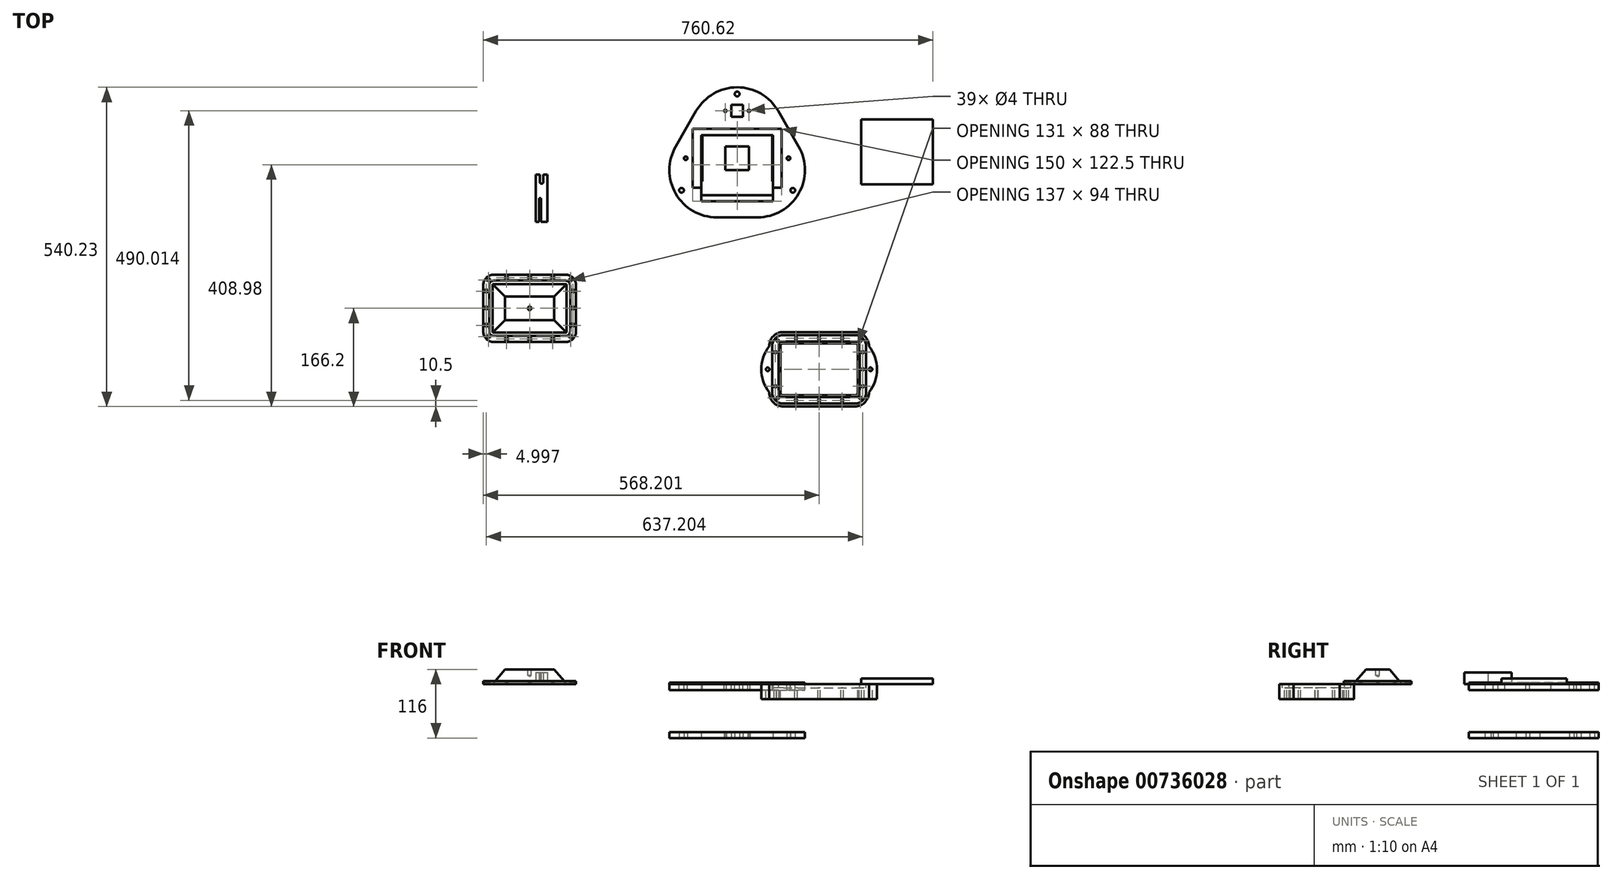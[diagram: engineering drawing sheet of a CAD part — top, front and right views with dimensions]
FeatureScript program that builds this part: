
annotation { "Feature Type Name" : "Feature", "Feature Type Description" : "" }
export const myFeature = defineFeature(function(context is Context, id is Id, definition is map)
    precondition{}
    {
        {
            var Q0;
            Q0=qCreatedBy(makeId("Top.planeOp"),FACE);
            var sketch = newSketch(context, id + "F0", { "sketchPlane" : qUnion([Q0])});
            skLineSegment(sketch, "E0.bottom", {"start": v(-60.5, 39) * mm, "end": v(60.5, 39) * mm});
            skLineSegment(sketch, "E0.top", {"start": v(-60.5, -39) * mm, "end": v(60.5, -39) * mm});
            skLineSegment(sketch, "E0.left", {"start": v(-60.5, 39) * mm, "end": v(-60.5, -39) * mm});
            skLineSegment(sketch, "E0.right", {"start": v(60.5, 39) * mm, "end": v(60.5, -39) * mm});
            skLineSegment(sketch, "E1.bottom", {"start": v(75, -50) * mm, "end": v(-75, -50) * mm});
            skLineSegment(sketch, "E1.top", {"start": v(75, 50) * mm, "end": v(-75, 50) * mm});
            skLineSegment(sketch, "E1.left", {"start": v(75, -50) * mm, "end": v(75, 50) * mm});
            skLineSegment(sketch, "E1.right", {"start": v(-75, -50) * mm, "end": v(-75, 50) * mm});
            skCircle(sketch, "E2.cCircle", {"center": v(0, 0) * mm, "radius": 100 * mm, "construction": true});
            skLineSegment(sketch, "E2.0", {"start": v(34.64, -100) * mm, "end": v(-34.64, -100) * mm});
            skLineSegment(sketch, "E2.1", {"start": v(-103.92, 20) * mm, "end": v(-69.28, 80) * mm});
            skLineSegment(sketch, "E2.2", {"start": v(69.28, 80) * mm, "end": v(103.92, 20) * mm});
            skPoint(sketch, "E2.0.midPoint", {"position": v(0, -100) * mm});
            skPoint(sketch, "E3.visualSharp", {"position": v(-173.2, -100) * mm});
            skArc(sketch, "E3.filletArc", {"start": v(-103.92, 20) * mm, "mid": v(-103.92, -60) * mm, "end": v(-34.64, -100) * mm});
            skPoint(sketch, "E4.visualSharp", {"position": v(0, 200) * mm});
            skArc(sketch, "E4.filletArc", {"start": v(69.28, 80) * mm, "mid": v(0, 120) * mm, "end": v(-69.28, 80) * mm});
            skPoint(sketch, "E5.visualSharp", {"position": v(173.2, -100) * mm});
            skArc(sketch, "E5.filletArc", {"start": v(34.64, -100) * mm, "mid": v(103.92, -60) * mm, "end": v(103.92, 20) * mm});
            skLineSegment(sketch, "E6.bottom", {"start": v(10, 90.28) * mm, "end": v(-10, 90.28) * mm});
            skLineSegment(sketch, "E6.top", {"start": v(10, 70.28) * mm, "end": v(-10, 70.28) * mm});
            skLineSegment(sketch, "E6.left", {"start": v(10, 90.28) * mm, "end": v(10, 70.28) * mm});
            skLineSegment(sketch, "E6.right", {"start": v(-10, 90.28) * mm, "end": v(-10, 70.28) * mm});
            skPoint(sketch, "E6.middle", {"position": v(0, 80.28) * mm});
            skLineSegment(sketch, "E7", {"start": v(-57.27, -42.57) * mm, "end": v(57.28, -42.57) * mm, "construction": true});
            skLineSegment(sketch, "E8", {"start": v(0, -42.57) * mm, "end": v(0, -39) * mm, "construction": true});
            skLineSegment(sketch, "E9.0", {"start": v(-59, 39) * mm, "end": v(-59, -39) * mm});
            skLineSegment(sketch, "E10.0", {"start": v(59, 39) * mm, "end": v(59, -39) * mm});
            skCircle(sketch, "E11", {"center": v(87, 0) * mm, "radius": 3 * mm});
            skLineSegment(sketch, "E12.bottom", {"start": v(210.03, 65.62) * mm, "end": v(331.03, 65.62) * mm});
            skLineSegment(sketch, "E12.top", {"start": v(210.03, -44.38) * mm, "end": v(331.03, -44.38) * mm});
            skLineSegment(sketch, "E12.left", {"start": v(210.03, 65.62) * mm, "end": v(210.03, -44.38) * mm});
            skLineSegment(sketch, "E12.right", {"start": v(331.03, 65.62) * mm, "end": v(331.03, -44.38) * mm});
            skLineSegment(sketch, "E13.bottom", {"start": v(78.11, -313.23) * mm, "end": v(199.11, -313.23) * mm});
            skLineSegment(sketch, "E13.top", {"start": v(78.11, -401.23) * mm, "end": v(199.11, -401.23) * mm});
            skLineSegment(sketch, "E13.left", {"start": v(73.11, -318.23) * mm, "end": v(73.11, -396.23) * mm});
            skLineSegment(sketch, "E13.right", {"start": v(204.11, -318.23) * mm, "end": v(204.11, -396.23) * mm});
            skCircle(sketch, "E14", {"center": v(225.61, -357.23) * mm, "radius": 3 * mm});
            skPoint(sketch, "E14.centerSnap0", {"position": v(204.11, -357.23) * mm});
            skPoint(sketch, "E15", {"position": v(138.61, -357.23) * mm});
            skPoint(sketch, "E15.positionSnap0", {"position": v(138.61, -313.23) * mm});
            skPoint(sketch, "E15.positionSnap1", {"position": v(73.11, -357.23) * mm});
            skPoint(sketch, "E16.visualSharp", {"position": v(73.11, -313.23) * mm});
            skArc(sketch, "E16.filletArc", {"start": v(78.11, -313.23) * mm, "mid": v(74.58, -314.7) * mm, "end": v(73.11, -318.23) * mm});
            skPoint(sketch, "E17.visualSharp", {"position": v(73.11, -401.23) * mm});
            skArc(sketch, "E17.filletArc", {"start": v(73.11, -396.23) * mm, "mid": v(74.58, -399.77) * mm, "end": v(78.11, -401.23) * mm});
            skPoint(sketch, "E18.visualSharp", {"position": v(204.11, -401.23) * mm});
            skArc(sketch, "E18.filletArc", {"start": v(199.11, -401.23) * mm, "mid": v(202.65, -399.77) * mm, "end": v(204.11, -396.23) * mm});
            skPoint(sketch, "E19.visualSharp", {"position": v(204.11, -313.23) * mm});
            skArc(sketch, "E19.filletArc", {"start": v(204.11, -318.23) * mm, "mid": v(202.65, -314.7) * mm, "end": v(199.11, -313.23) * mm});
            skArc(sketch, "E20.0", {"start": v(78.11, -310.23) * mm, "mid": v(72.45, -312.57) * mm, "end": v(70.11, -318.23) * mm});
            skLineSegment(sketch, "E20.1", {"start": v(70.11, -318.23) * mm, "end": v(70.11, -396.23) * mm});
            skLineSegment(sketch, "E20.2", {"start": v(78.11, -310.23) * mm, "end": v(199.11, -310.23) * mm});
            skArc(sketch, "E20.3", {"start": v(70.11, -396.23) * mm, "mid": v(72.45, -401.89) * mm, "end": v(78.11, -404.23) * mm});
            skArc(sketch, "E20.4", {"start": v(207.11, -318.23) * mm, "mid": v(204.77, -312.57) * mm, "end": v(199.11, -310.23) * mm});
            skLineSegment(sketch, "E20.5", {"start": v(207.11, -318.23) * mm, "end": v(207.11, -396.23) * mm});
            skArc(sketch, "E20.6", {"start": v(199.11, -404.23) * mm, "mid": v(204.77, -401.89) * mm, "end": v(207.11, -396.23) * mm});
            skLineSegment(sketch, "E20.7", {"start": v(78.11, -404.23) * mm, "end": v(199.11, -404.23) * mm});
            skArc(sketch, "E21.0", {"start": v(78.11, -299.23) * mm, "mid": v(64.68, -304.8) * mm, "end": v(59.11, -318.23) * mm});
            skLineSegment(sketch, "E21.1", {"start": v(59.11, -318.23) * mm, "end": v(59.11, -396.23) * mm});
            skLineSegment(sketch, "E21.2", {"start": v(78.11, -299.23) * mm, "end": v(199.11, -299.23) * mm});
            skArc(sketch, "E21.3", {"start": v(59.11, -396.23) * mm, "mid": v(64.68, -409.66) * mm, "end": v(78.11, -415.23) * mm});
            skArc(sketch, "E21.4", {"start": v(218.11, -318.23) * mm, "mid": v(212.55, -304.8) * mm, "end": v(199.11, -299.23) * mm});
            skLineSegment(sketch, "E21.5", {"start": v(218.11, -318.23) * mm, "end": v(218.11, -396.23) * mm});
            skArc(sketch, "E21.6", {"start": v(199.11, -415.23) * mm, "mid": v(212.55, -409.66) * mm, "end": v(218.11, -396.23) * mm});
            skLineSegment(sketch, "E21.7", {"start": v(78.11, -415.23) * mm, "end": v(199.11, -415.23) * mm});
            skArc(sketch, "E22.0", {"start": v(78.11, -294.23) * mm, "mid": v(61.14, -301.26) * mm, "end": v(54.11, -318.23) * mm});
            skLineSegment(sketch, "E22.1", {"start": v(54.11, -318.23) * mm, "end": v(54.11, -396.23) * mm});
            skLineSegment(sketch, "E22.2", {"start": v(78.11, -294.23) * mm, "end": v(199.11, -294.23) * mm});
            skArc(sketch, "E22.3", {"start": v(54.11, -396.23) * mm, "mid": v(61.14, -413.2) * mm, "end": v(78.11, -420.23) * mm});
            skArc(sketch, "E22.4", {"start": v(223.11, -318.23) * mm, "mid": v(216.08, -301.26) * mm, "end": v(199.11, -294.23) * mm});
            skLineSegment(sketch, "E22.5", {"start": v(223.11, -318.23) * mm, "end": v(223.11, -396.23) * mm});
            skArc(sketch, "E22.6", {"start": v(199.11, -420.23) * mm, "mid": v(216.08, -413.2) * mm, "end": v(223.11, -396.23) * mm});
            skLineSegment(sketch, "E22.7", {"start": v(78.11, -420.23) * mm, "end": v(199.11, -420.23) * mm});
            skArc(sketch, "E23", {"start": v(223.11, -396.23) * mm, "mid": v(236.56, -357.23) * mm, "end": v(223.11, -318.23) * mm});
            skLineSegment(sketch, "E24", {"start": v(138.61, -357.23) * mm, "end": v(138.61, -335.81) * mm, "construction": true});
            skCircle(sketch, "E25.MirrorC", {"center": v(51.61, -357.23) * mm, "radius": 3 * mm});
            skArc(sketch, "E26.MirrorCS", {"start": v(54.11, -396.23) * mm, "mid": v(40.66, -357.23) * mm, "end": v(54.11, -318.23) * mm});
            skArc(sketch, "E27.0", {"start": v(212.61, -318.23) * mm, "mid": v(208.66, -308.68) * mm, "end": v(199.11, -304.73) * mm, "construction": true});
            skLineSegment(sketch, "E27.1", {"start": v(78.11, -304.73) * mm, "end": v(138.61, -304.73) * mm, "construction": true});
            skLineSegment(sketch, "E27.2", {"start": v(212.61, -318.23) * mm, "end": v(212.61, -357.23) * mm, "construction": true});
            skArc(sketch, "E27.3", {"start": v(78.11, -304.73) * mm, "mid": v(68.56, -308.68) * mm, "end": v(64.61, -318.23) * mm, "construction": true});
            skArc(sketch, "E27.4", {"start": v(199.11, -409.73) * mm, "mid": v(208.66, -405.78) * mm, "end": v(212.61, -396.23) * mm, "construction": true});
            skLineSegment(sketch, "E27.5", {"start": v(78.11, -409.73) * mm, "end": v(138.61, -409.73) * mm, "construction": true});
            skArc(sketch, "E27.6", {"start": v(64.61, -396.23) * mm, "mid": v(68.56, -405.78) * mm, "end": v(78.11, -409.73) * mm, "construction": true});
            skLineSegment(sketch, "E27.7", {"start": v(64.61, -318.23) * mm, "end": v(64.61, -357.23) * mm, "construction": true});
            skPoint(sketch, "E28", {"position": v(208.66, -405.78) * mm});
            skPoint(sketch, "E29", {"position": v(212.61, -357.23) * mm});
            skPoint(sketch, "E30", {"position": v(138.61, -409.73) * mm});
            skPoint(sketch, "E31", {"position": v(64.61, -357.23) * mm});
            skPoint(sketch, "E32", {"position": v(68.56, -405.78) * mm});
            skPoint(sketch, "E33", {"position": v(208.66, -308.68) * mm});
            skPoint(sketch, "E34", {"position": v(68.56, -308.68) * mm});
            skPoint(sketch, "E35", {"position": v(138.61, -304.73) * mm});
            skLineSegment(sketch, "E36", {"start": v(64.61, -357.23) * mm, "end": v(64.61, -396.23) * mm, "construction": true});
            skLineSegment(sketch, "E37", {"start": v(138.61, -409.73) * mm, "end": v(199.11, -409.73) * mm, "construction": true});
            skLineSegment(sketch, "E38", {"start": v(212.61, -357.23) * mm, "end": v(212.61, -396.23) * mm, "construction": true});
            skLineSegment(sketch, "E39", {"start": v(138.61, -304.73) * mm, "end": v(199.11, -304.73) * mm, "construction": true});
            skPoint(sketch, "E40", {"position": v(177.68, -304.73) * mm});
            skPoint(sketch, "E41.MirrorP", {"position": v(99.54, -304.73) * mm});
            skLineSegment(sketch, "E42", {"start": v(138.61, -357.23) * mm, "end": v(162.86, -357.23) * mm, "construction": true});
            skPoint(sketch, "E43", {"position": v(212.61, -328.33) * mm});
            skPoint(sketch, "E44.MirrorP", {"position": v(212.61, -386.12) * mm});
            skPoint(sketch, "E45.MirrorP", {"position": v(177.68, -409.73) * mm});
            skPoint(sketch, "E46.MirrorP", {"position": v(99.54, -409.73) * mm});
            skPoint(sketch, "E47.MirrorP", {"position": v(64.61, -328.33) * mm});
            skPoint(sketch, "E48.MirrorP", {"position": v(64.61, -386.12) * mm});
            skLineSegment(sketch, "E49.bottom", {"start": v(-411.6, -210.03) * mm, "end": v(-290.6, -210.03) * mm});
            skLineSegment(sketch, "E49.top", {"start": v(-411.6, -298.03) * mm, "end": v(-290.6, -298.03) * mm});
            skLineSegment(sketch, "E49.left", {"start": v(-416.6, -215.03) * mm, "end": v(-416.6, -293.03) * mm});
            skLineSegment(sketch, "E49.right", {"start": v(-285.6, -215.03) * mm, "end": v(-285.6, -293.03) * mm});
            skCircle(sketch, "E50", {"center": v(-264.1, -254.03) * mm, "radius": 3 * mm});
            skPoint(sketch, "E50.centerSnap0", {"position": v(-285.6, -254.03) * mm});
            skPoint(sketch, "E51", {"position": v(-351.1, -254.03) * mm});
            skPoint(sketch, "E51.positionSnap0", {"position": v(-351.1, -210.03) * mm});
            skPoint(sketch, "E51.positionSnap1", {"position": v(-416.6, -254.03) * mm});
            skPoint(sketch, "E52.visualSharp", {"position": v(-416.6, -210.03) * mm});
            skArc(sketch, "E52.filletArc", {"start": v(-411.6, -210.03) * mm, "mid": v(-415.13, -211.5) * mm, "end": v(-416.6, -215.03) * mm});
            skPoint(sketch, "E53.visualSharp", {"position": v(-416.6, -298.03) * mm});
            skArc(sketch, "E53.filletArc", {"start": v(-416.6, -293.03) * mm, "mid": v(-415.13, -296.57) * mm, "end": v(-411.6, -298.03) * mm});
            skPoint(sketch, "E54.visualSharp", {"position": v(-285.6, -298.03) * mm});
            skArc(sketch, "E54.filletArc", {"start": v(-290.6, -298.03) * mm, "mid": v(-287.06, -296.57) * mm, "end": v(-285.6, -293.03) * mm});
            skPoint(sketch, "E55.visualSharp", {"position": v(-285.6, -210.03) * mm});
            skArc(sketch, "E55.filletArc", {"start": v(-285.6, -215.03) * mm, "mid": v(-287.06, -211.5) * mm, "end": v(-290.6, -210.03) * mm});
            skArc(sketch, "E56.0", {"start": v(-411.6, -207.03) * mm, "mid": v(-417.25, -209.37) * mm, "end": v(-419.6, -215.03) * mm});
            skLineSegment(sketch, "E56.1", {"start": v(-419.6, -215.03) * mm, "end": v(-419.6, -293.03) * mm});
            skLineSegment(sketch, "E56.2", {"start": v(-411.6, -207.03) * mm, "end": v(-290.6, -207.03) * mm});
            skArc(sketch, "E56.3", {"start": v(-419.6, -293.03) * mm, "mid": v(-417.25, -298.69) * mm, "end": v(-411.6, -301.03) * mm});
            skArc(sketch, "E56.4", {"start": v(-282.6, -215.03) * mm, "mid": v(-284.94, -209.37) * mm, "end": v(-290.6, -207.03) * mm});
            skLineSegment(sketch, "E56.5", {"start": v(-282.6, -215.03) * mm, "end": v(-282.6, -293.03) * mm});
            skArc(sketch, "E56.6", {"start": v(-290.6, -301.03) * mm, "mid": v(-284.94, -298.69) * mm, "end": v(-282.6, -293.03) * mm});
            skLineSegment(sketch, "E56.7", {"start": v(-411.6, -301.03) * mm, "end": v(-290.6, -301.03) * mm});
            skArc(sketch, "E57.0", {"start": v(-411.6, -197.03) * mm, "mid": v(-424.32, -202.3) * mm, "end": v(-429.6, -215.03) * mm});
            skLineSegment(sketch, "E57.1", {"start": v(-429.6, -215.03) * mm, "end": v(-429.6, -293.03) * mm});
            skLineSegment(sketch, "E57.2", {"start": v(-411.6, -197.03) * mm, "end": v(-290.6, -197.03) * mm});
            skArc(sketch, "E57.3", {"start": v(-429.6, -293.03) * mm, "mid": v(-424.32, -305.76) * mm, "end": v(-411.6, -311.03) * mm});
            skArc(sketch, "E57.4", {"start": v(-272.6, -215.03) * mm, "mid": v(-277.87, -202.3) * mm, "end": v(-290.6, -197.03) * mm});
            skLineSegment(sketch, "E57.5", {"start": v(-272.6, -215.03) * mm, "end": v(-272.6, -293.03) * mm});
            skArc(sketch, "E57.6", {"start": v(-290.6, -311.03) * mm, "mid": v(-277.87, -305.76) * mm, "end": v(-272.6, -293.03) * mm});
            skLineSegment(sketch, "E57.7", {"start": v(-411.6, -311.03) * mm, "end": v(-290.6, -311.03) * mm});
            skArc(sketch, "E58.0", {"start": v(-411.6, -192.03) * mm, "mid": v(-427.86, -198.77) * mm, "end": v(-434.6, -215.03) * mm});
            skLineSegment(sketch, "E58.1", {"start": v(-434.6, -215.03) * mm, "end": v(-434.6, -293.03) * mm});
            skLineSegment(sketch, "E58.2", {"start": v(-411.6, -192.03) * mm, "end": v(-290.6, -192.03) * mm});
            skArc(sketch, "E58.3", {"start": v(-434.6, -293.03) * mm, "mid": v(-427.86, -309.3) * mm, "end": v(-411.6, -316.03) * mm});
            skArc(sketch, "E58.4", {"start": v(-267.6, -215.03) * mm, "mid": v(-274.33, -198.77) * mm, "end": v(-290.6, -192.03) * mm});
            skLineSegment(sketch, "E58.5", {"start": v(-267.6, -215.03) * mm, "end": v(-267.6, -293.03) * mm});
            skArc(sketch, "E58.6", {"start": v(-290.6, -316.03) * mm, "mid": v(-274.33, -309.3) * mm, "end": v(-267.6, -293.03) * mm});
            skLineSegment(sketch, "E58.7", {"start": v(-411.6, -316.03) * mm, "end": v(-290.6, -316.03) * mm});
            skArc(sketch, "E59", {"start": v(-267.6, -293.03) * mm, "mid": v(-254.14, -254.03) * mm, "end": v(-267.6, -215.03) * mm});
            skLineSegment(sketch, "E60", {"start": v(-351.1, -254.03) * mm, "end": v(-351.1, -232.61) * mm, "construction": true});
            skCircle(sketch, "E61.MirrorC", {"center": v(-438.1, -254.03) * mm, "radius": 3 * mm});
            skArc(sketch, "E62.MirrorCS", {"start": v(-434.6, -293.03) * mm, "mid": v(-448.04, -254.03) * mm, "end": v(-434.6, -215.03) * mm});
            skArc(sketch, "E63.0", {"start": v(-277.6, -215.03) * mm, "mid": v(-281.4, -205.84) * mm, "end": v(-290.6, -202.03) * mm, "construction": true});
            skLineSegment(sketch, "E63.1", {"start": v(-411.6, -202.03) * mm, "end": v(-351.1, -202.03) * mm, "construction": true});
            skLineSegment(sketch, "E63.2", {"start": v(-277.6, -215.03) * mm, "end": v(-277.6, -254.03) * mm, "construction": true});
            skArc(sketch, "E63.3", {"start": v(-411.6, -202.03) * mm, "mid": v(-420.79, -205.84) * mm, "end": v(-424.6, -215.03) * mm, "construction": true});
            skArc(sketch, "E63.4", {"start": v(-290.6, -306.03) * mm, "mid": v(-281.4, -302.22) * mm, "end": v(-277.6, -293.03) * mm, "construction": true});
            skLineSegment(sketch, "E63.5", {"start": v(-411.6, -306.03) * mm, "end": v(-351.1, -306.03) * mm, "construction": true});
            skArc(sketch, "E63.6", {"start": v(-424.6, -293.03) * mm, "mid": v(-420.79, -302.22) * mm, "end": v(-411.6, -306.03) * mm, "construction": true});
            skLineSegment(sketch, "E63.7", {"start": v(-424.6, -215.03) * mm, "end": v(-424.6, -254.03) * mm, "construction": true});
            skPoint(sketch, "E64", {"position": v(-281.4, -302.22) * mm});
            skPoint(sketch, "E65", {"position": v(-277.6, -254.03) * mm});
            skPoint(sketch, "E66", {"position": v(-351.1, -306.03) * mm});
            skPoint(sketch, "E67", {"position": v(-424.6, -254.03) * mm});
            skPoint(sketch, "E68", {"position": v(-420.79, -302.22) * mm});
            skPoint(sketch, "E69", {"position": v(-281.4, -205.84) * mm});
            skPoint(sketch, "E70", {"position": v(-420.79, -205.84) * mm});
            skPoint(sketch, "E71", {"position": v(-351.1, -202.03) * mm});
            skLineSegment(sketch, "E72", {"start": v(-424.6, -254.03) * mm, "end": v(-424.6, -293.03) * mm, "construction": true});
            skLineSegment(sketch, "E73", {"start": v(-351.1, -306.03) * mm, "end": v(-290.6, -306.03) * mm, "construction": true});
            skLineSegment(sketch, "E74", {"start": v(-277.6, -254.03) * mm, "end": v(-277.6, -293.03) * mm, "construction": true});
            skLineSegment(sketch, "E75", {"start": v(-351.1, -202.03) * mm, "end": v(-290.6, -202.03) * mm, "construction": true});
            skPoint(sketch, "E76", {"position": v(-312.03, -202.03) * mm});
            skPoint(sketch, "E77.MirrorP", {"position": v(-390.16, -202.03) * mm});
            skLineSegment(sketch, "E78", {"start": v(-351.1, -254.03) * mm, "end": v(-326.85, -254.03) * mm, "construction": true});
            skPoint(sketch, "E79", {"position": v(-277.6, -225.14) * mm});
            skPoint(sketch, "E80.MirrorP", {"position": v(-277.6, -282.93) * mm});
            skPoint(sketch, "E81.MirrorP", {"position": v(-312.03, -306.03) * mm});
            skPoint(sketch, "E82.MirrorP", {"position": v(-390.16, -306.03) * mm});
            skPoint(sketch, "E83.MirrorP", {"position": v(-424.6, -225.14) * mm});
            skPoint(sketch, "E84.MirrorP", {"position": v(-424.6, -282.93) * mm});
            skLineSegment(sketch, "E85", {"start": v(0, 0) * mm, "end": v(0, -20.47) * mm, "construction": true});
            skCircle(sketch, "E86.MirrorC", {"center": v(-87, 0) * mm, "radius": 3 * mm});
            skCircle(sketch, "E87", {"center": v(0, 108.66) * mm, "radius": 4 * mm});
            skPoint(sketch, "E87.centerSnap0", {"position": v(0, 90.28) * mm});
            skCircle(sketch, "E88.1.0", {"center": v(-94.1, -54.33) * mm, "radius": 4 * mm});
            skCircle(sketch, "E88.2.0", {"center": v(94.1, -54.33) * mm, "radius": 4 * mm});
            skPoint(sketch, "E89", {"position": v(-20, 80.28) * mm});
            skPoint(sketch, "E89.positionSnap0", {"position": v(-10, 80.28) * mm});
            skPoint(sketch, "E90", {"position": v(20, 80.28) * mm});
            skPoint(sketch, "E90.positionSnap0", {"position": v(10, 80.28) * mm});
            skCircle(sketch, "E91", {"center": v(20, 80.28) * mm, "radius": 2 * mm});
            skCircle(sketch, "E92", {"center": v(-20, 80.28) * mm, "radius": 2 * mm});
            skLineSegment(sketch, "E93.0", {"start": v(-413.6, -213.03) * mm, "end": v(-413.6, -295.03) * mm});
            skLineSegment(sketch, "E93.1", {"start": v(-413.6, -213.03) * mm, "end": v(-288.6, -213.03) * mm});
            skLineSegment(sketch, "E93.2", {"start": v(-288.6, -213.03) * mm, "end": v(-288.6, -295.03) * mm});
            skLineSegment(sketch, "E93.3", {"start": v(-413.6, -295.03) * mm, "end": v(-288.6, -295.03) * mm});
            skLineSegment(sketch, "E94.bottom", {"start": v(-340.93, -107.54) * mm, "end": v(-320.93, -107.54) * mm});
            skLineSegment(sketch, "E94.top", {"start": v(-340.93, -27.54) * mm, "end": v(-320.93, -27.54) * mm});
            skLineSegment(sketch, "E94.left", {"start": v(-340.93, -107.54) * mm, "end": v(-340.93, -27.54) * mm});
            skLineSegment(sketch, "E94.right", {"start": v(-320.93, -107.54) * mm, "end": v(-320.93, -27.54) * mm});
            skPoint(sketch, "E95.oppositeSnap0", {"position": v(-320.93, -67.54) * mm});
            skLineSegment(sketch, "E95.bottom", {"start": v(-334.9, -107.54) * mm, "end": v(-331.9, -107.54) * mm});
            skLineSegment(sketch, "E95.top", {"start": v(-334.9, -67.54) * mm, "end": v(-331.9, -67.54) * mm});
            skLineSegment(sketch, "E95.left", {"start": v(-334.9, -107.54) * mm, "end": v(-334.9, -67.54) * mm});
            skLineSegment(sketch, "E95.right", {"start": v(-331.9, -107.54) * mm, "end": v(-331.9, -67.54) * mm});
            skCircle(sketch, "E96", {"center": v(-330.93, -40.04) * mm, "radius": 3 * mm});
            skPoint(sketch, "E96.centerSnap0", {"position": v(-330.93, -27.54) * mm});
            skCircle(sketch, "E97.0.1.0", {"center": v(-330.93, -39.54) * mm, "radius": 3 * mm});
            skCircle(sketch, "E97.0.2.0", {"center": v(-330.93, -39.04) * mm, "radius": 3 * mm});
            skCircle(sketch, "E97.0.3.0", {"center": v(-330.93, -38.54) * mm, "radius": 3 * mm});
            skCircle(sketch, "E97.0.4.0", {"center": v(-330.93, -38.04) * mm, "radius": 3 * mm});
            skCircle(sketch, "E97.0.5.0", {"center": v(-330.93, -37.54) * mm, "radius": 3 * mm});
            skCircle(sketch, "E97.0.6.0", {"center": v(-330.93, -37.04) * mm, "radius": 3 * mm});
            skCircle(sketch, "E97.0.7.0", {"center": v(-330.93, -36.54) * mm, "radius": 3 * mm});
            skCircle(sketch, "E97.0.8.0", {"center": v(-330.93, -36.04) * mm, "radius": 3 * mm});
            skCircle(sketch, "E97.0.9.0", {"center": v(-330.93, -35.54) * mm, "radius": 3 * mm});
            skCircle(sketch, "E97.0.10.0", {"center": v(-330.93, -35.04) * mm, "radius": 3 * mm});
            skCircle(sketch, "E97.0.11.0", {"center": v(-330.93, -34.54) * mm, "radius": 3 * mm});
            skCircle(sketch, "E97.0.12.0", {"center": v(-330.93, -34.04) * mm, "radius": 3 * mm});
            skCircle(sketch, "E97.0.13.0", {"center": v(-330.93, -33.54) * mm, "radius": 3 * mm});
            skCircle(sketch, "E97.0.14.0", {"center": v(-330.93, -33.04) * mm, "radius": 3 * mm});
            skCircle(sketch, "E97.0.15.0", {"center": v(-330.93, -32.54) * mm, "radius": 3 * mm});
            skCircle(sketch, "E97.0.16.0", {"center": v(-330.93, -32.04) * mm, "radius": 3 * mm});
            skCircle(sketch, "E97.0.17.0", {"center": v(-330.93, -31.54) * mm, "radius": 3 * mm});
            skCircle(sketch, "E97.0.18.0", {"center": v(-330.93, -31.04) * mm, "radius": 3 * mm});
            skCircle(sketch, "E97.0.19.0", {"center": v(-330.93, -30.54) * mm, "radius": 3 * mm});
            skCircle(sketch, "E97.0.20.0", {"center": v(-330.93, -30.04) * mm, "radius": 3 * mm});
            skCircle(sketch, "E97.0.21.0", {"center": v(-330.93, -29.54) * mm, "radius": 3 * mm});
            skCircle(sketch, "E97.0.22.0", {"center": v(-330.93, -29.04) * mm, "radius": 3 * mm});
            skCircle(sketch, "E97.0.23.0", {"center": v(-330.93, -28.54) * mm, "radius": 3 * mm});
            skCircle(sketch, "E97.0.24.0", {"center": v(-330.93, -28.04) * mm, "radius": 3 * mm});
            skCircle(sketch, "E97.0.25.0", {"center": v(-330.93, -27.54) * mm, "radius": 3 * mm});
            skCircle(sketch, "E97.0.26.0", {"center": v(-330.93, -27.04) * mm, "radius": 3 * mm});
            skCircle(sketch, "E97.0.27.0", {"center": v(-330.93, -26.54) * mm, "radius": 3 * mm});
            skCircle(sketch, "E97.0.28.0", {"center": v(-330.93, -26.04) * mm, "radius": 3 * mm});
            skCircle(sketch, "E97.0.29.0", {"center": v(-330.93, -25.54) * mm, "radius": 3 * mm});
            skLineSegment(sketch, "E97.direction1", {"start": v(-330.93, -40.04) * mm, "end": v(-305.93, -40.04) * mm, "construction": true});
            skLineSegment(sketch, "E97.direction2", {"start": v(-330.93, -40.04) * mm, "end": v(-330.93, -39.54) * mm, "construction": true});
            skSolve(sketch);
        }
        {
            var Q0;
            Q0=makeQuery(id+"F0.imprint","IMPRINT",FACE,{"disambiguationData":[TD([[makeQuery(id+"F0.imprint","IMPRINT",EDGE,{"derivedFrom":sQuery(id+"F0.wireOp",EDGE,"E1.bottom")}),1.0]])]});
            var Q1;
            {var subQ1=sQuery(id+"F0.wireOp",EDGE,"E0.left");Q1=makeQuery(id+"F0.imprint","IMPRINT",FACE,{"disambiguationData":[TD([[makeQuery(id+"F0.imprint","IMPRINT",EDGE,{"derivedFrom":subQ1}),-1.0]])]});}
            var Q2;
            {var subQ0=sQuery(id+"F0.wireOp",EDGE,"E0.left");Q2=makeQuery(id+"F0.imprint","IMPRINT",FACE,{"disambiguationData":[TD([[makeQuery(id+"F0.imprint","IMPRINT",EDGE,{"derivedFrom":subQ0}),1.0]])]});}
            var Q3;
            {var subQ0=sQuery(id+"F0.wireOp",EDGE,"E0.right");Q3=makeQuery(id+"F0.imprint","IMPRINT",FACE,{"disambiguationData":[TD([[makeQuery(id+"F0.imprint","IMPRINT",EDGE,{"derivedFrom":subQ0}),-1.0]])]});}
            extrude(context, id + "F1", {"entities" : qUnion([Q0, Q1, Q2, Q3]), "oppositeDirection" : true, "depth" : 10 * mm, "offsetDistance" : 25 * mm});
        }
        {
            var Q0;
            Q0=makeQuery(id+"F0.imprint","IMPRINT",FACE,{"disambiguationData":[TD([[makeQuery(id+"F0.imprint","IMPRINT",EDGE,{"derivedFrom":sQuery(id+"F0.wireOp",EDGE,"E1.bottom")}),1.0]])]});
            var Q1;
            {var subQ1=sQuery(id+"F0.wireOp",EDGE,"E0.left");Q1=makeQuery(id+"F0.imprint","IMPRINT",FACE,{"disambiguationData":[TD([[makeQuery(id+"F0.imprint","IMPRINT",EDGE,{"derivedFrom":subQ1}),-1.0]])]});}
            extrude(context, id + "F2", {"entities" : qUnion([Q0, Q1]), "depth" : 1 * mm, "offsetDistance" : 25 * mm});
        }
        {
            var Q0;
            Q0=makeQuery(id+"F0.imprint","IMPRINT",FACE,{"disambiguationData":[TD([[makeQuery(id+"F0.imprint","IMPRINT",EDGE,{"derivedFrom":sQuery(id+"F0.wireOp",EDGE,"E1.bottom")}),1.0]])]});
            extrude(context, id + "F3", {"entities" : qUnion([Q0]), "depth" : 3 * mm, "offsetDistance" : 25 * mm, "hasSecondDirection" : true, "secondDirectionOppositeDirection" : false, "secondDirectionDepth" : 1 * mm});
        }
        {
            var Q0;
            Q0=makeQuery(id+"F0.imprint","IMPRINT",FACE,{"disambiguationData":[TD([[makeQuery(id+"F0.imprint","IMPRINT",EDGE,{"derivedFrom":sQuery(id+"F0.wireOp",EDGE,"E12.bottom")}),-1.0]])]});
            extrude(context, id + "F4", {"entities" : qUnion([Q0]), "depth" : 10 * mm, "offsetDistance" : 25 * mm});
        }
        {
            var Q0;
            Q0=makeQuery(id+"F1.opExtrude","CAP_FACE",FACE,{"disambiguationData":[OSD([sQuery(id+"F0.wireOp",EDGE,"E0.bottom"),sQuery(id+"F0.wireOp",EDGE,"E0.top"),sQuery(id+"F0.wireOp",EDGE,"E2.0"),sQuery(id+"F0.wireOp",EDGE,"E2.1"),sQuery(id+"F0.wireOp",EDGE,"E2.2"),sQuery(id+"F0.wireOp",EDGE,"E3.filletArc"),sQuery(id+"F0.wireOp",EDGE,"E4.filletArc"),sQuery(id+"F0.wireOp",EDGE,"E5.filletArc"),sQuery(id+"F0.wireOp",EDGE,"E6.bottom"),sQuery(id+"F0.wireOp",EDGE,"E6.top"),sQuery(id+"F0.wireOp",EDGE,"E6.left"),sQuery(id+"F0.wireOp",EDGE,"E6.right"),sQuery(id+"F0.wireOp",EDGE,"E9.0"),sQuery(id+"F0.wireOp",EDGE,"E10.0"),sQuery(id+"F0.wireOp",EDGE,"E11")])],"isStart":false});
            var sketch = newSketch(context, id + "F5", { "sketchPlane" : qUnion([Q0])});
            skLineSegment(sketch, "E98.bottom", {"start": v(60.5, 62.5) * mm, "end": v(-60.5, 62.5) * mm, "construction": true});
            skLineSegment(sketch, "E98.top", {"start": v(60.5, 72.5) * mm, "end": v(-60.5, 72.5) * mm});
            skLineSegment(sketch, "E98.left", {"start": v(60.5, 62.5) * mm, "end": v(60.5, 72.5) * mm});
            skLineSegment(sketch, "E98.right", {"start": v(-60.5, 62.5) * mm, "end": v(-60.5, 72.5) * mm});
            skPoint(sketch, "E98.middle", {"position": v(0, 67.5) * mm});
            skLineSegment(sketch, "E99.top", {"start": v(-60.5, 39) * mm, "end": v(60.5, 39) * mm});
            skLineSegment(sketch, "E99.left", {"start": v(-60.5, 62.5) * mm, "end": v(-60.5, 39) * mm});
            skLineSegment(sketch, "E99.right", {"start": v(60.5, 62.5) * mm, "end": v(60.5, 39) * mm});
            skSolve(sketch);
        }
        {
            var Q0;
            Q0=makeQuery(id+"F0.imprint","IMPRINT",FACE,{"disambiguationData":[TD([[makeQuery(id+"F0.imprint","IMPRINT",EDGE,{"derivedFrom":sQuery(id+"F0.wireOp",EDGE,"E22.1")}),-1.0]])]});
            var Q1;
            Q1=makeQuery(id+"F0.imprint","IMPRINT",FACE,{"disambiguationData":[TD([[makeQuery(id+"F0.imprint","IMPRINT",EDGE,{"derivedFrom":sQuery(id+"F0.wireOp",EDGE,"E21.0")}),-1.0]])]});
            var Q2;
            Q2=makeQuery(id+"F0.imprint","IMPRINT",FACE,{"disambiguationData":[TD([[makeQuery(id+"F0.imprint","IMPRINT",EDGE,{"derivedFrom":sQuery(id+"F0.wireOp",EDGE,"E20.0")}),-1.0]])]});
            var Q3;
            Q3=makeQuery(id+"F0.imprint","IMPRINT",FACE,{"disambiguationData":[TD([[makeQuery(id+"F0.imprint","IMPRINT",EDGE,{"derivedFrom":sQuery(id+"F0.wireOp",EDGE,"E13.bottom")}),1.0]])]});
            var Q4;
            Q4=makeQuery(id+"F0.imprint","IMPRINT",FACE,{"disambiguationData":[TD([[makeQuery(id+"F0.imprint","IMPRINT",EDGE,{"derivedFrom":sQuery(id+"F0.wireOp",EDGE,"E14")}),-1.0]])]});
            extrude(context, id + "F6", {"entities" : qUnion([Q0, Q1, Q2, Q3, Q4]), "oppositeDirection" : true, "depth" : 25 * mm, "offsetDistance" : 25 * mm});
        }
        {
            var Q0;
            Q0=makeQuery(id+"F0.imprint","IMPRINT",FACE,{"disambiguationData":[TD([[makeQuery(id+"F0.imprint","IMPRINT",EDGE,{"derivedFrom":sQuery(id+"F0.wireOp",EDGE,"E20.0")}),-1.0]])]});
            extrude(context, id + "F7", {"entities" : qUnion([Q0]), "operationType" : NewBodyOperationType.REMOVE, "oppositeDirection" : true, "depth" : 6 * mm, "offsetDistance" : 25 * mm});
        }
        {
            var Q0;
            Q0=sQuery(id+"F0.wireOp",VERTEX,"E34");
            var Q1;
            Q1=sQuery(id+"F0.wireOp",VERTEX,"E41.MirrorP");
            var Q2;
            Q2=sQuery(id+"F0.wireOp",VERTEX,"E35");
            var Q3;
            Q3=sQuery(id+"F0.wireOp",VERTEX,"E40");
            var Q4;
            Q4=sQuery(id+"F0.wireOp",VERTEX,"E33");
            var Q5;
            Q5=sQuery(id+"F0.wireOp",VERTEX,"E43");
            var Q6;
            Q6=sQuery(id+"F0.wireOp",VERTEX,"E29");
            var Q7;
            Q7=sQuery(id+"F0.wireOp",VERTEX,"E44.MirrorP");
            var Q8;
            Q8=sQuery(id+"F0.wireOp",VERTEX,"E28");
            var Q9;
            Q9=sQuery(id+"F0.wireOp",VERTEX,"E45.MirrorP");
            var Q10;
            Q10=sQuery(id+"F0.wireOp",VERTEX,"E30");
            var Q11;
            Q11=sQuery(id+"F0.wireOp",VERTEX,"E46.MirrorP");
            var Q12;
            Q12=sQuery(id+"F0.wireOp",VERTEX,"E32");
            var Q13;
            Q13=sQuery(id+"F0.wireOp",VERTEX,"E48.MirrorP");
            var Q14;
            Q14=sQuery(id+"F0.wireOp",VERTEX,"E47.MirrorP");
            var Q15;
            Q15=makeQuery(id+"F6.opExtrude","SWEPT_BODY",BODY,{"disambiguationData":[OSD([sQuery(id+"F0.wireOp",EDGE,"E13.bottom"),sQuery(id+"F0.wireOp",EDGE,"E13.top"),sQuery(id+"F0.wireOp",EDGE,"E13.left"),sQuery(id+"F0.wireOp",EDGE,"E13.right"),sQuery(id+"F0.wireOp",EDGE,"E14"),sQuery(id+"F0.wireOp",EDGE,"E16.filletArc"),sQuery(id+"F0.wireOp",EDGE,"E17.filletArc"),sQuery(id+"F0.wireOp",EDGE,"E18.filletArc"),sQuery(id+"F0.wireOp",EDGE,"E19.filletArc"),sQuery(id+"F0.wireOp",EDGE,"E22.0"),sQuery(id+"F0.wireOp",EDGE,"E22.2"),sQuery(id+"F0.wireOp",EDGE,"E22.3"),sQuery(id+"F0.wireOp",EDGE,"E22.4"),sQuery(id+"F0.wireOp",EDGE,"E22.6"),sQuery(id+"F0.wireOp",EDGE,"E22.7"),sQuery(id+"F0.wireOp",EDGE,"E23"),sQuery(id+"F0.wireOp",EDGE,"E25.MirrorC"),sQuery(id+"F0.wireOp",EDGE,"E26.MirrorCS")])]});
            hole(context, id + "F8", {"style" : HoleStyle.SIMPLE, "endStyle" : HoleEndStyle.THROUGH, "holeDiameter" : 4 * mm, "majorDiameter" : 5 * mm, "isTappedThrough" : true, "tappedDepth" : 12 * mm, "tapClearance" : 3, "startFromSketch" : true, "locations" : qUnion([Q0, Q1, Q2, Q3, Q4, Q5, Q6, Q7, Q8, Q9, Q10, Q11, Q12, Q13, Q14]), "scope" : qUnion([Q15])});
        }
        {
            var Q0;
            Q0=makeQuery(id+"F0.imprint","IMPRINT",FACE,{"disambiguationData":[TD([[makeQuery(id+"F0.imprint","IMPRINT",EDGE,{"derivedFrom":sQuery(id+"F0.wireOp",EDGE,"E56.0")}),-1.0]])]});
            extrude(context, id + "F9", {"entities" : qUnion([Q0]), "depth" : 5 * mm, "offsetDistance" : 25 * mm});
        }
        {
            var Q0;
            Q0=sQuery(id+"F0.wireOp",VERTEX,"E70");
            var Q1;
            Q1=sQuery(id+"F0.wireOp",VERTEX,"E77.MirrorP");
            var Q2;
            Q2=sQuery(id+"F0.wireOp",VERTEX,"E71");
            var Q3;
            Q3=sQuery(id+"F0.wireOp",VERTEX,"E83.MirrorP");
            var Q4;
            Q4=sQuery(id+"F0.wireOp",VERTEX,"E67");
            var Q5;
            Q5=sQuery(id+"F0.wireOp",VERTEX,"E84.MirrorP");
            var Q6;
            Q6=sQuery(id+"F0.wireOp",VERTEX,"E68");
            var Q7;
            Q7=sQuery(id+"F0.wireOp",VERTEX,"E82.MirrorP");
            var Q8;
            Q8=sQuery(id+"F0.wireOp",VERTEX,"E66");
            var Q9;
            Q9=sQuery(id+"F0.wireOp",VERTEX,"E81.MirrorP");
            var Q10;
            Q10=sQuery(id+"F0.wireOp",VERTEX,"E64");
            var Q11;
            Q11=sQuery(id+"F0.wireOp",VERTEX,"E80.MirrorP");
            var Q12;
            Q12=sQuery(id+"F0.wireOp",VERTEX,"E65");
            var Q13;
            Q13=sQuery(id+"F0.wireOp",VERTEX,"E79");
            var Q14;
            Q14=sQuery(id+"F0.wireOp",VERTEX,"E69");
            var Q15;
            Q15=sQuery(id+"F0.wireOp",VERTEX,"E76");
            var Q16;
            Q16=makeQuery(id+"F9.opExtrude","SWEPT_BODY",BODY,{"disambiguationData":[OSD([sQuery(id+"F0.wireOp",EDGE,"E56.0"),sQuery(id+"F0.wireOp",EDGE,"E56.1"),sQuery(id+"F0.wireOp",EDGE,"E56.2"),sQuery(id+"F0.wireOp",EDGE,"E56.3"),sQuery(id+"F0.wireOp",EDGE,"E56.4"),sQuery(id+"F0.wireOp",EDGE,"E56.5"),sQuery(id+"F0.wireOp",EDGE,"E56.6"),sQuery(id+"F0.wireOp",EDGE,"E56.7"),sQuery(id+"F0.wireOp",EDGE,"E57.0"),sQuery(id+"F0.wireOp",EDGE,"E57.1"),sQuery(id+"F0.wireOp",EDGE,"E57.2"),sQuery(id+"F0.wireOp",EDGE,"E57.3"),sQuery(id+"F0.wireOp",EDGE,"E57.4"),sQuery(id+"F0.wireOp",EDGE,"E57.5"),sQuery(id+"F0.wireOp",EDGE,"E57.6"),sQuery(id+"F0.wireOp",EDGE,"E57.7")])]});
            hole(context, id + "F10", {"style" : HoleStyle.C_SINK, "endStyle" : HoleEndStyle.THROUGH, "oppositeDirection" : true, "holeDiameter" : 4 * mm, "cSinkDiameter" : 8 * mm, "cSinkAngle" : 90 * degree, "majorDiameter" : 5 * mm, "isTappedThrough" : true, "tappedDepth" : 12 * mm, "tapClearance" : 3, "startFromSketch" : true, "locations" : qUnion([Q0, Q1, Q2, Q3, Q4, Q5, Q6, Q7, Q8, Q9, Q10, Q11, Q12, Q13, Q14, Q15]), "scope" : qUnion([Q16])});
        }
        {
            var Q0;
            Q0=makeQuery(id+"F5.imprint","IMPRINT",FACE,{"disambiguationData":[TD([[makeQuery(id+"F5.imprint","IMPRINT",EDGE,{"derivedFrom":sQuery(id+"F5.wireOp",EDGE,"E98.top")}),1.0]])]});
            extrude(context, id + "F11", {"entities" : qUnion([Q0]), "operationType" : NewBodyOperationType.REMOVE, "oppositeDirection" : true, "depth" : 25 * mm, "offsetDistance" : 25 * mm});
        }
        {
            var Q0;
            Q0=makeQuery(id+"F0.imprint","IMPRINT",FACE,{"disambiguationData":[TD([[makeQuery(id+"F0.imprint","IMPRINT",EDGE,{"derivedFrom":sQuery(id+"F0.wireOp",EDGE,"E1.bottom")}),1.0]])]});
            var Q1;
            {var subQ1=sQuery(id+"F0.wireOp",EDGE,"E0.left");Q1=makeQuery(id+"F0.imprint","IMPRINT",FACE,{"disambiguationData":[TD([[makeQuery(id+"F0.imprint","IMPRINT",EDGE,{"derivedFrom":subQ1}),-1.0]])]});}
            var Q2;
            {var subQ0=sQuery(id+"F0.wireOp",EDGE,"E9.0");Q2=makeQuery(id+"F0.imprint","IMPRINT",FACE,{"disambiguationData":[TD([[makeQuery(id+"F0.imprint","IMPRINT",EDGE,{"derivedFrom":subQ0}),1.0]])]});}
            var Q3;
            {var subQ0=sQuery(id+"F0.wireOp",EDGE,"E0.right");Q3=makeQuery(id+"F0.imprint","IMPRINT",FACE,{"disambiguationData":[TD([[makeQuery(id+"F0.imprint","IMPRINT",EDGE,{"derivedFrom":subQ0}),-1.0]])]});}
            var Q4;
            {var subQ0=sQuery(id+"F0.wireOp",EDGE,"E0.left");Q4=makeQuery(id+"F0.imprint","IMPRINT",FACE,{"disambiguationData":[TD([[makeQuery(id+"F0.imprint","IMPRINT",EDGE,{"derivedFrom":subQ0}),1.0]])]});}
            extrude(context, id + "F12", {"entities" : qUnion([Q0, Q1, Q2, Q3, Q4]), "depth" : 10 * mm, "offsetDistance" : 25 * mm});
        }
        {
            var Q0;
            Q0=makeQuery(id+"F12.opExtrude","SWEPT_BODY",BODY,{"disambiguationData":[OSD([sQuery(id+"F0.wireOp",EDGE,"E2.0"),sQuery(id+"F0.wireOp",EDGE,"E2.1"),sQuery(id+"F0.wireOp",EDGE,"E2.2"),sQuery(id+"F0.wireOp",EDGE,"E3.filletArc"),sQuery(id+"F0.wireOp",EDGE,"E4.filletArc"),sQuery(id+"F0.wireOp",EDGE,"E5.filletArc"),sQuery(id+"F0.wireOp",EDGE,"E6.bottom"),sQuery(id+"F0.wireOp",EDGE,"E6.top"),sQuery(id+"F0.wireOp",EDGE,"E6.left"),sQuery(id+"F0.wireOp",EDGE,"E6.right"),sQuery(id+"F0.wireOp",EDGE,"E11"),sQuery(id+"F0.wireOp",EDGE,"E86.MirrorC"),sQuery(id+"F0.wireOp",EDGE,"E87"),sQuery(id+"F0.wireOp",EDGE,"E88.1.0"),sQuery(id+"F0.wireOp",EDGE,"E88.2.0")])]});
            transform(context, id + "F13", {"entities" : qUnion([Q0]), "transformType" : TransformType.TRANSLATION_3D, "dx" : 0 * mm, "dy" : 0 * mm, "dz" : -91 * mm, "makeCopy" : false});
        }
        {
            var Q0;
            Q0=makeQuery(id+"F12.opExtrude","CAP_FACE",FACE,{"disambiguationData":[OSD([sQuery(id+"F0.wireOp",EDGE,"E2.0"),sQuery(id+"F0.wireOp",EDGE,"E2.1"),sQuery(id+"F0.wireOp",EDGE,"E2.2"),sQuery(id+"F0.wireOp",EDGE,"E3.filletArc"),sQuery(id+"F0.wireOp",EDGE,"E4.filletArc"),sQuery(id+"F0.wireOp",EDGE,"E5.filletArc"),sQuery(id+"F0.wireOp",EDGE,"E6.bottom"),sQuery(id+"F0.wireOp",EDGE,"E6.top"),sQuery(id+"F0.wireOp",EDGE,"E6.left"),sQuery(id+"F0.wireOp",EDGE,"E6.right"),sQuery(id+"F0.wireOp",EDGE,"E11"),sQuery(id+"F0.wireOp",EDGE,"E86.MirrorC"),sQuery(id+"F0.wireOp",EDGE,"E87"),sQuery(id+"F0.wireOp",EDGE,"E88.1.0"),sQuery(id+"F0.wireOp",EDGE,"E88.2.0")])],"isStart":true});
            var sketch = newSketch(context, id + "F14", { "sketchPlane" : qUnion([Q0])});
            skLineSegment(sketch, "E100.bottom", {"start": v(-20, -20) * mm, "end": v(20, -20) * mm});
            skLineSegment(sketch, "E100.top", {"start": v(-20, 20) * mm, "end": v(20, 20) * mm});
            skLineSegment(sketch, "E100.left", {"start": v(-20, -20) * mm, "end": v(-20, 20) * mm});
            skLineSegment(sketch, "E100.right", {"start": v(20, -20) * mm, "end": v(20, 20) * mm});
            skPoint(sketch, "E100.middle", {"position": v(0, 0) * mm});
            skLineSegment(sketch, "E101.top", {"start": v(60.5, 72.5) * mm, "end": v(-60.5, 72.5) * mm});
            skLineSegment(sketch, "E101.left", {"start": v(60.5, 62.5) * mm, "end": v(60.5, 72.5) * mm});
            skLineSegment(sketch, "E101.right", {"start": v(-60.5, 62.5) * mm, "end": v(-60.5, 72.5) * mm});
            skLineSegment(sketch, "E102.top", {"start": v(-60.5, 34.42) * mm, "end": v(60.5, 34.42) * mm});
            skLineSegment(sketch, "E103", {"start": v(60.5, 62.5) * mm, "end": v(-60.5, 62.5) * mm});
            skSolve(sketch);
        }
        {
            var Q0;
            Q0=makeQuery(id+"F14.imprint","IMPRINT",FACE,{"disambiguationData":[TD([[makeQuery(id+"F14.imprint","IMPRINT",EDGE,{"derivedFrom":sQuery(id+"F14.wireOp",EDGE,"E100.bottom")}),1.0]])]});
            var Q1;
            Q1=makeQuery(id+"F14.imprint","IMPRINT",FACE,{"disambiguationData":[TD([[makeQuery(id+"F14.imprint","IMPRINT",EDGE,{"derivedFrom":sQuery(id+"F14.wireOp",EDGE,"E101.top")}),1.0]])]});
            extrude(context, id + "F15", {"entities" : qUnion([Q0, Q1]), "operationType" : NewBodyOperationType.REMOVE, "oppositeDirection" : true, "depth" : 25 * mm, "offsetDistance" : 25 * mm});
        }
        {
            var Q0;
            Q0=makeQuery(id+"F0.imprint","IMPRINT",FACE,{"disambiguationData":[TD([[makeQuery(id+"F0.imprint","IMPRINT",EDGE,{"derivedFrom":sQuery(id+"F0.wireOp",EDGE,"E93.0")}),1.0]])]});
            extrude(context, id + "F16", {"entities" : qUnion([Q0]), "depth" : 25 * mm, "offsetDistance" : 25 * mm, "hasDraft" : true, "draftAngle" : 40 * degree, "draftPullDirection" : true});
        }
        {
            var Q0;
            Q0=makeQuery(id+"F16.opExtrude","CAP_FACE",FACE,{"disambiguationData":[OSD([sQuery(id+"F0.wireOp",EDGE,"E93.0"),sQuery(id+"F0.wireOp",EDGE,"E93.1"),sQuery(id+"F0.wireOp",EDGE,"E93.2"),sQuery(id+"F0.wireOp",EDGE,"E93.3")])],"isStart":false});
            var sketch = newSketch(context, id + "F17", { "sketchPlane" : qUnion([Q0])});
            skPoint(sketch, "E104", {"position": v(-351.1, -254.03) * mm});
            skPoint(sketch, "E104.positionSnap0", {"position": v(-351.1, -274.05) * mm});
            skPoint(sketch, "E104.positionSnap1", {"position": v(-392.62, -254.03) * mm});
            skSolve(sketch);
        }
        {
            var Q0;
            Q0=sQuery(id+"F17.wireOp",VERTEX,"E104");
            var Q1;
            Q1=makeQuery(id+"F16.opExtrude","SWEPT_BODY",BODY,{"disambiguationData":[OSD([sQuery(id+"F0.wireOp",EDGE,"E93.0"),sQuery(id+"F0.wireOp",EDGE,"E93.1"),sQuery(id+"F0.wireOp",EDGE,"E93.2"),sQuery(id+"F0.wireOp",EDGE,"E93.3")])]});
            hole(context, id + "F18", {"style" : HoleStyle.SIMPLE, "endStyle" : HoleEndStyle.BLIND, "holeDiameter" : 6 * mm, "majorDiameter" : 5 * mm, "holeDepth" : 10 * mm, "isTappedThrough" : true, "tappedDepth" : 12 * mm, "tapClearance" : 3, "startFromSketch" : true, "locations" : qUnion([Q0]), "scope" : qUnion([Q1])});
        }
        {
            var Q0;
            {var subQ59=sQuery(id+"F0.wireOp",EDGE,"E94.left");Q0=makeQuery(id+"F0.imprint","IMPRINT",FACE,{"disambiguationData":[TD([[makeQuery(id+"F0.imprint","IMPRINT",EDGE,{"derivedFrom":subQ59}),-1.0]])]});}
            extrude(context, id + "F19", {"entities" : qUnion([Q0]), "depth" : 20 * mm, "offsetDistance" : 25 * mm});
        }
    });
